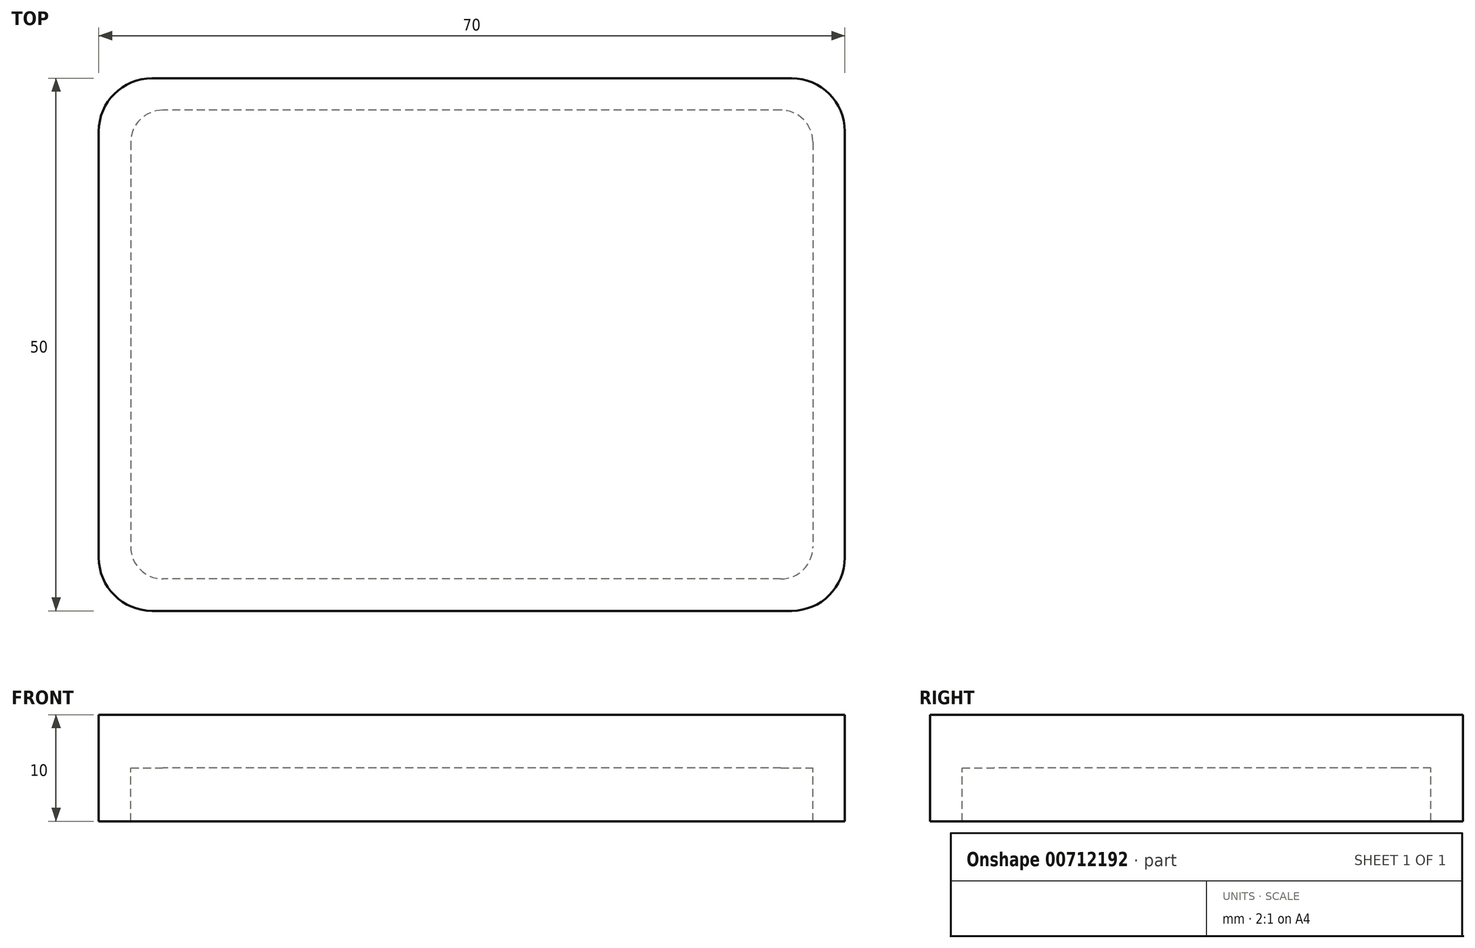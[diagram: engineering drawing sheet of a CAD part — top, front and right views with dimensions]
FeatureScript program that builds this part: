
annotation { "Feature Type Name" : "Feature", "Feature Type Description" : "" }
export const myFeature = defineFeature(function(context is Context, id is Id, definition is map)
    precondition{}
    {
        {
            var Q0;
            Q0=qCreatedBy(makeId("Top.planeOp"),FACE);
            var sketch = newSketch(context, id + "F0", { "sketchPlane" : qUnion([Q0])});
            skLineSegment(sketch, "E0.bottom", {"start": v(30, 25) * mm, "end": v(-30, 25) * mm});
            skLineSegment(sketch, "E0.top", {"start": v(30, -25) * mm, "end": v(-30, -25) * mm});
            skLineSegment(sketch, "E0.left", {"start": v(35, 20) * mm, "end": v(35, -20) * mm});
            skLineSegment(sketch, "E0.right", {"start": v(-35, 20) * mm, "end": v(-35, -20) * mm});
            skPoint(sketch, "E0.middle", {"position": v(0, 0) * mm});
            skPoint(sketch, "E1.visualSharp", {"position": v(-35, 25) * mm});
            skArc(sketch, "E1.filletArc", {"start": v(-30, 25) * mm, "mid": v(-33.54, 23.54) * mm, "end": v(-35, 20) * mm});
            skPoint(sketch, "E2.visualSharp", {"position": v(35, 25) * mm});
            skArc(sketch, "E2.filletArc", {"start": v(35, 20) * mm, "mid": v(33.54, 23.54) * mm, "end": v(30, 25) * mm});
            skPoint(sketch, "E3.visualSharp", {"position": v(35, -25) * mm});
            skArc(sketch, "E3.filletArc", {"start": v(30, -25) * mm, "mid": v(33.54, -23.54) * mm, "end": v(35, -20) * mm});
            skPoint(sketch, "E4.visualSharp", {"position": v(-35, -25) * mm});
            skArc(sketch, "E4.filletArc", {"start": v(-35, -20) * mm, "mid": v(-33.54, -23.54) * mm, "end": v(-30, -25) * mm});
            skLineSegment(sketch, "E5.0", {"start": v(-32, 19) * mm, "end": v(-32, -19) * mm});
            skLineSegment(sketch, "E5.1", {"start": v(29, 22) * mm, "end": v(-29, 22) * mm});
            skLineSegment(sketch, "E5.2", {"start": v(32, 19) * mm, "end": v(32, -19) * mm});
            skLineSegment(sketch, "E5.3", {"start": v(29, -22) * mm, "end": v(-29, -22) * mm});
            skPoint(sketch, "E6.visualSharp", {"position": v(32, 22) * mm});
            skArc(sketch, "E6.filletArc", {"start": v(32, 19) * mm, "mid": v(31.12, 21.12) * mm, "end": v(29, 22) * mm});
            skPoint(sketch, "E7.visualSharp", {"position": v(32, -22) * mm});
            skArc(sketch, "E7.filletArc", {"start": v(29, -22) * mm, "mid": v(31.12, -21.12) * mm, "end": v(32, -19) * mm});
            skPoint(sketch, "E8.visualSharp", {"position": v(-32, -22) * mm});
            skArc(sketch, "E8.filletArc", {"start": v(-32, -19) * mm, "mid": v(-31.12, -21.12) * mm, "end": v(-29, -22) * mm});
            skPoint(sketch, "E9.visualSharp", {"position": v(-32, 22) * mm});
            skArc(sketch, "E9.filletArc", {"start": v(-29, 22) * mm, "mid": v(-31.12, 21.12) * mm, "end": v(-32, 19) * mm});
            skSolve(sketch);
        }
        {
            var Q0;
            Q0=makeQuery(id+"F0.imprint","IMPRINT",FACE,{"disambiguationData":[TD([[makeQuery(id+"F0.imprint","IMPRINT",EDGE,{"derivedFrom":sQuery(id+"F0.wireOp",EDGE,"E0.bottom")}),1.0]])]});
            var Q1;
            Q1=makeQuery(id+"F0.imprint","IMPRINT",FACE,{"disambiguationData":[TD([[makeQuery(id+"F0.imprint","IMPRINT",EDGE,{"derivedFrom":sQuery(id+"F0.wireOp",EDGE,"E5.0")}),1.0]])]});
            extrude(context, id + "F1", {"entities" : qUnion([Q0, Q1]), "depth" : 5 * mm, "offsetDistance" : 25 * mm});
        }
        {
            var Q0;
            Q0=makeQuery(id+"F0.imprint","IMPRINT",FACE,{"disambiguationData":[TD([[makeQuery(id+"F0.imprint","IMPRINT",EDGE,{"derivedFrom":sQuery(id+"F0.wireOp",EDGE,"E0.bottom")}),1.0]])]});
            extrude(context, id + "F2", {"entities" : qUnion([Q0]), "operationType" : NewBodyOperationType.ADD, "oppositeDirection" : true, "depth" : 5 * mm, "offsetDistance" : 25 * mm});
        }
    });
